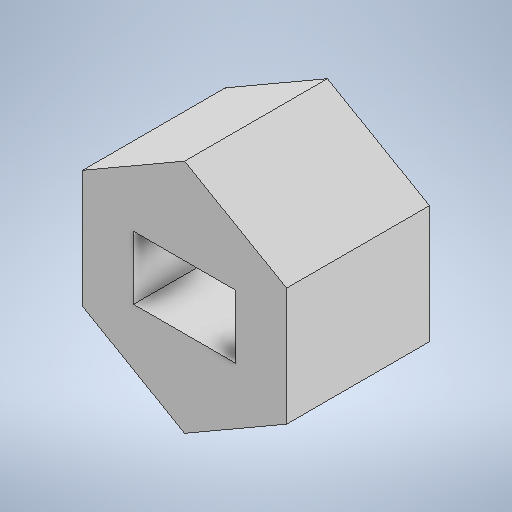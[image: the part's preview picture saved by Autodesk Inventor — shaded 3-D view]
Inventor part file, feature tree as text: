
AUTODESK INVENTOR PART (.ipt)
format: ipt  version: 2025.3 (Build 293356000, 356)  size: 198,656 bytes
history: native  units: mm
features: other x1, extrude x1, sketch x1
ambient origin geometry x8: Origin, YZ Plane, XZ Plane, XY Plane, X Axis, Y Axis, Z Axis, Center Point
bodies: Body1 (feature_tree)
feature tree (3):
  other  "ソリッド1"
  extrude  "押し出し1"  Depth=10.0mm
  sketch  "スケッチ1"
